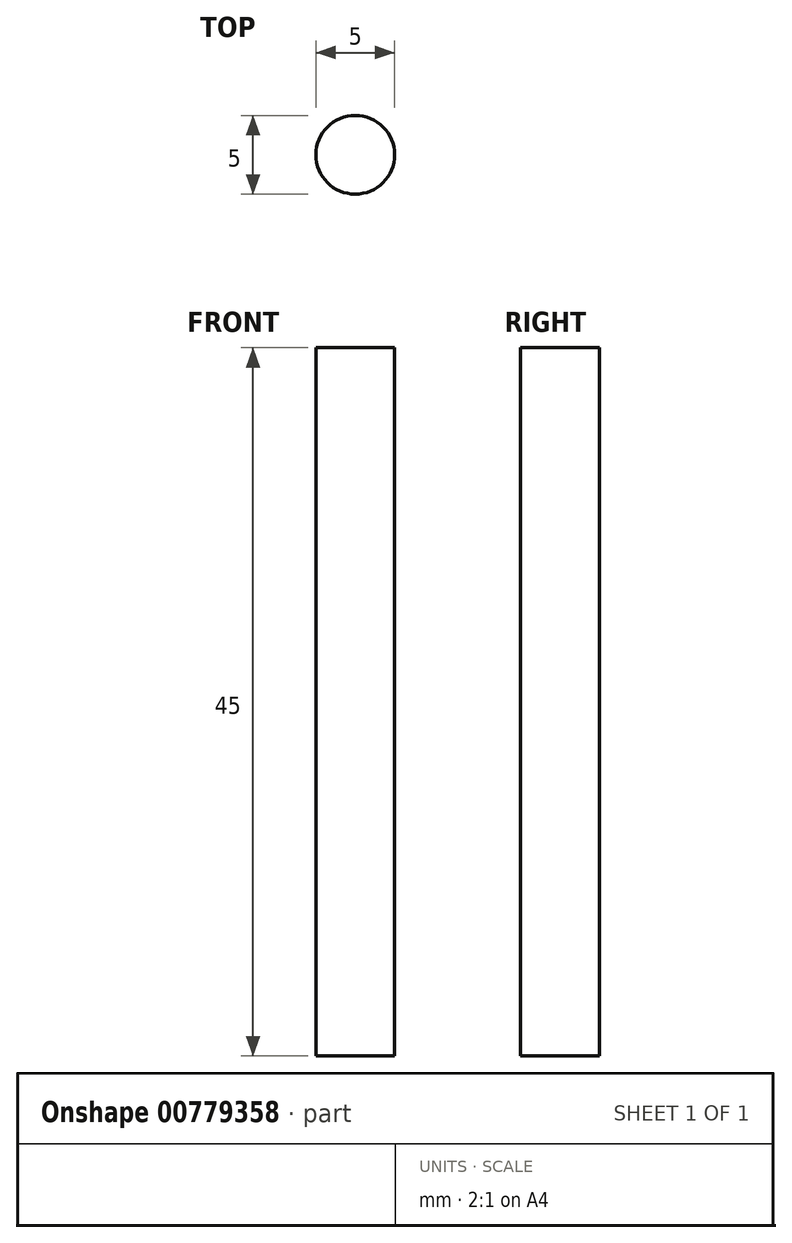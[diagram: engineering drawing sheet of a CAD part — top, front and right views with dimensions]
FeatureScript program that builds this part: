
annotation { "Feature Type Name" : "Feature", "Feature Type Description" : "" }
export const myFeature = defineFeature(function(context is Context, id is Id, definition is map)
    precondition{}
    {
        {
            var Q0;
            Q0=qCreatedBy(makeId("Top.planeOp"),FACE);
            var sketch = newSketch(context, id + "F0", { "sketchPlane" : qUnion([Q0])});
            skCircle(sketch, "E0", {"center": v(0, 0) * mm, "radius": 2.5 * mm});
            skSolve(sketch);
        }
        {
            var Q0;
            Q0=makeQuery(id+"F0.imprint","IMPRINT",FACE,{"disambiguationData":[TD([[makeQuery(id+"F0.imprint","IMPRINT",EDGE,{"derivedFrom":sQuery(id+"F0.wireOp",EDGE,"E0")}),1.0]])]});
            extrude(context, id + "F1", {"entities" : qUnion([Q0]), "flatOperationType" : FlatOperationType.REMOVE, "depth" : 45 * mm, "offsetDistance" : 25 * mm, "domain" : OperationDomain.MODEL});
        }
    });
